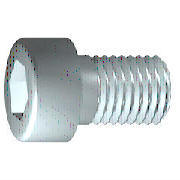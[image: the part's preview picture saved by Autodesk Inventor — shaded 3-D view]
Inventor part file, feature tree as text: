
AUTODESK INVENTOR PART (.ipt)
format: ipt  version: 2017 (Build 210142000, 142)  size: 183,808 bytes
history: native  units: mm (DEFAULTED — no unit token found)
features: sketch x2, extrude x1, plane x1, fillet x1
ambient origin geometry x7: Origin, YZ Plane, XY Plane, X Axis, Y Axis, Z Axis, Center Point
bodies: Solid1 (feature_tree), Body (feature_tree)
feature tree (5):
  extrude  "Slot"  Depth=5.0mm
  plane  "Work Plane1"
  fillet  "Fillet2"  Radius=5.0mm
  sketch  "Sketch1"  dims[d1=22.0mm d2=0.49086mm d3=5.0mm]
  sketch  "Sketch2"  dims[d4=2.5mm d5=60.0deg d6=5.0mm d7=5.0mm d8=4.618802mm d9=8.5mm d10=90.0deg d11=10.0mm d12=0.0mm d13=22.0mm d14=0.0mm d15=0.49076mm d16=0.49076mm d17=0.5mm d19=0.0mm d26=60.0mm d27=45.0deg d28=0.0mm d29=0.0mm d30=0.1mm]
